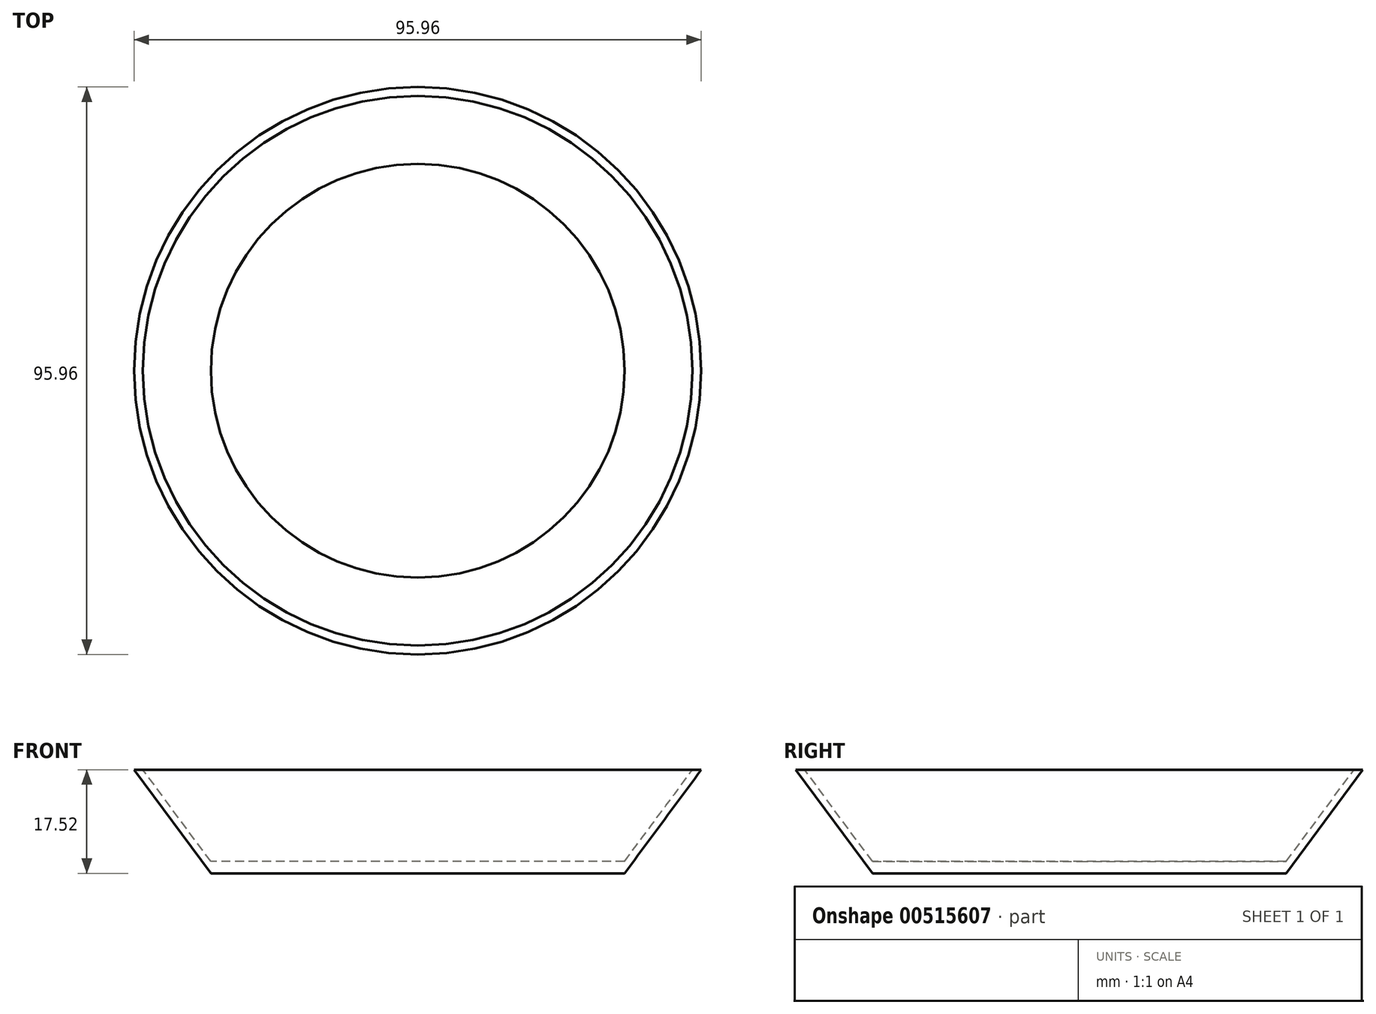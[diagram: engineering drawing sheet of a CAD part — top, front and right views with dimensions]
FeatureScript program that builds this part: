
annotation { "Feature Type Name" : "Feature", "Feature Type Description" : "" }
export const myFeature = defineFeature(function(context is Context, id is Id, definition is map)
    precondition{}
    {
        {
            var Q0;
            Q0=qCreatedBy(makeId("Front.planeOp"),FACE);
            var sketch = newSketch(context, id + "F0", { "sketchPlane" : qUnion([Q0])});
            skLineSegment(sketch, "E0.bottom", {"start": v(-44.47, -7.68) * mm, "end": v(-9.47, -7.68) * mm});
            skLineSegment(sketch, "E0.top", {"start": v(-44.47, -9.68) * mm, "end": v(-9.47, -9.68) * mm});
            skLineSegment(sketch, "E0.left", {"start": v(-44.47, -7.68) * mm, "end": v(-44.47, -9.68) * mm});
            skLineSegment(sketch, "E0.right", {"start": v(-9.47, -7.68) * mm, "end": v(-9.47, -9.68) * mm});
            skLineSegment(sketch, "E1", {"start": v(-44.47, -7.68) * mm, "end": v(-55.97, 7.84) * mm});
            skLineSegment(sketch, "E2", {"start": v(-44.47, -9.68) * mm, "end": v(-57.45, 7.84) * mm});
            skLineSegment(sketch, "E3", {"start": v(-55.97, 7.84) * mm, "end": v(-57.45, 7.84) * mm});
            skSolve(sketch);
        }
        {
            var Q0;
            Q0=makeQuery(id+"F0.imprint","IMPRINT",FACE,{"disambiguationData":[TD([[makeQuery(id+"F0.imprint","IMPRINT",EDGE,{"derivedFrom":sQuery(id+"F0.wireOp",EDGE,"E0.left")}),-1.0]])]});
            var Q1;
            Q1=makeQuery(id+"F0.imprint","IMPRINT",FACE,{"disambiguationData":[TD([[makeQuery(id+"F0.imprint","IMPRINT",EDGE,{"derivedFrom":sQuery(id+"F0.wireOp",EDGE,"E0.bottom")}),-1.0]])]});
            var Q2;
            Q2=sQuery(id+"F0.wireOp",EDGE,"E0.right");
            revolve(context, id + "F1", {"entities" : qUnion([Q0, Q1]), "axis" : qUnion([Q2]), "revolveType" : RevolveType.FULL});
        }
    });
